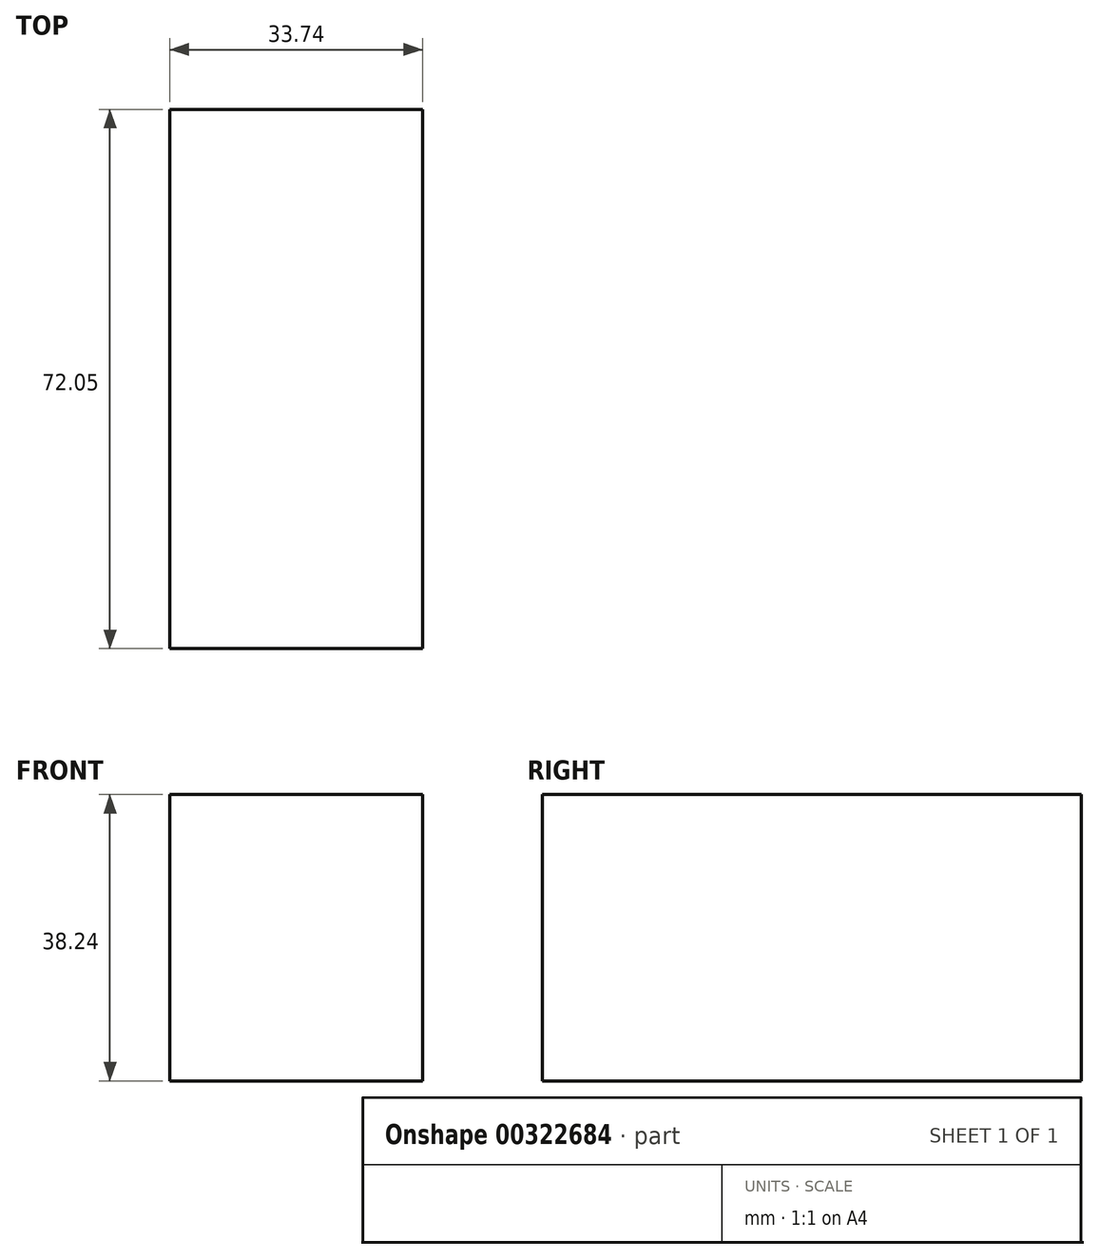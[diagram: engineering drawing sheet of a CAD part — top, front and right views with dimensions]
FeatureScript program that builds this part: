
annotation { "Feature Type Name" : "Feature", "Feature Type Description" : "" }
export const myFeature = defineFeature(function(context is Context, id is Id, definition is map)
    precondition{}
    {
        {
            var Q0;
            Q0=qCreatedBy(makeId("Front.planeOp"),FACE);
            var sketch = newSketch(context, id + "F0", { "sketchPlane" : qUnion([Q0])});
            skLineSegment(sketch, "E0.bottom", {"start": v(-33.74, 38.24) * mm, "end": v(0, 38.24) * mm});
            skLineSegment(sketch, "E0.top", {"start": v(-33.74, 0) * mm, "end": v(0, 0) * mm});
            skLineSegment(sketch, "E0.left", {"start": v(-33.74, 38.24) * mm, "end": v(-33.74, 0) * mm});
            skLineSegment(sketch, "E0.right", {"start": v(0, 38.24) * mm, "end": v(0, 0) * mm});
            skSolve(sketch);
        }
        {
            var Q0;
            Q0=makeQuery(id+"F0.imprint","IMPRINT",FACE,{"disambiguationData":[TD([[makeQuery(id+"F0.imprint","IMPRINT",EDGE,{"derivedFrom":sQuery(id+"F0.wireOp",EDGE,"E0.bottom")}),-1.0]])]});
            extrude(context, id + "F1", {"entities" : qUnion([Q0]), "depth" : 72.05 * mm});
        }
    });
